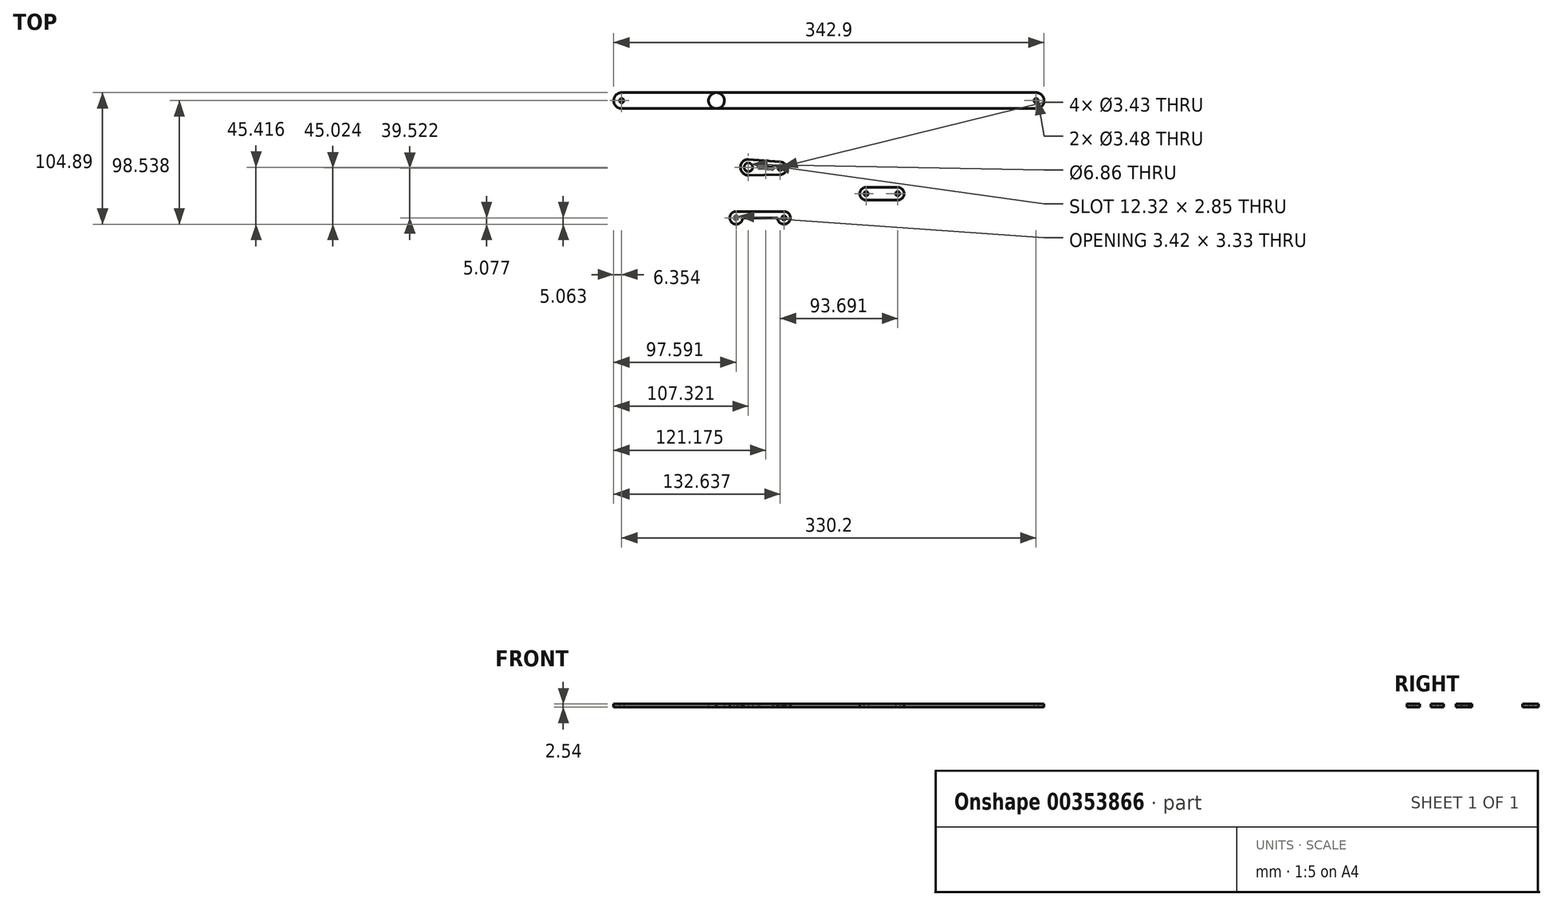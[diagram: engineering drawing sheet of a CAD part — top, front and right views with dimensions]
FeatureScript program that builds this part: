
annotation { "Feature Type Name" : "Feature", "Feature Type Description" : "" }
export const myFeature = defineFeature(function(context is Context, id is Id, definition is map)
    precondition{}
    {
        {
            var Q0;
            Q0=qCreatedBy(makeId("Top.planeOp"),FACE);
            var sketch = newSketch(context, id + "F0", { "sketchPlane" : qUnion([Q0])});
            skLineSegment(sketch, "E0", {"start": v(-140.79, 34.4) * mm, "end": v(189.41, 34.4) * mm});
            skCircle(sketch, "E1", {"center": v(-65.23, 34.4) * mm, "radius": 6.35 * mm});
            skCircle(sketch, "E2", {"center": v(-140.79, 34.4) * mm, "radius": 6.35 * mm});
            skCircle(sketch, "E3", {"center": v(189.41, 34.4) * mm, "radius": 6.35 * mm});
            skCircle(sketch, "E4", {"center": v(-140.79, 34.4) * mm, "radius": 1.74 * mm});
            skCircle(sketch, "E5", {"center": v(-65.23, 34.4) * mm, "radius": 1.74 * mm});
            skCircle(sketch, "E6", {"center": v(189.41, 34.4) * mm, "radius": 1.74 * mm});
            skLineSegment(sketch, "E7", {"start": v(-140.74, 40.75) * mm, "end": v(-65.23, 40.75) * mm});
            skLineSegment(sketch, "E8", {"start": v(-65.23, 40.75) * mm, "end": v(189.41, 40.75) * mm});
            skLineSegment(sketch, "E9", {"start": v(-140.79, 28.05) * mm, "end": v(189.41, 28.05) * mm});
            skSolve(sketch);
        }
        {
            var Q0;
            {var subQ5=sQuery(id+"F0.wireOp",EDGE,"omyWqJSU-xpnl-p9V4-5C7R-NGolSmvEfpRZ");Q0=makeQuery(id+"F0.imprint","IMPRINT",FACE,{"disambiguationData":[TD([[makeQuery(id+"F0.imprint","IMPRINT",EDGE,{"derivedFrom":subQ5}),-1.0]])]});}
            var Q1;
            {var subQ5=sQuery(id+"F0.wireOp",EDGE,"3vT1Dh1F-cFY9-jmHm-KNHv-sDzjYtVH3cF0");Q1=makeQuery(id+"F0.imprint","IMPRINT",FACE,{"disambiguationData":[TD([[makeQuery(id+"F0.imprint","IMPRINT",EDGE,{"derivedFrom":subQ5}),-1.0]])]});}
            var Q2;
            {var subQ5=sQuery(id+"F0.wireOp",EDGE,"hbOdxzbA-R3wx-VJPs-SB4o-o1RYoFjZylJU");Q2=makeQuery(id+"F0.imprint","IMPRINT",FACE,{"disambiguationData":[TD([[makeQuery(id+"F0.imprint","IMPRINT",EDGE,{"derivedFrom":subQ5}),1.0]])]});}
            var Q3;
            {var subQ5=sQuery(id+"F0.wireOp",EDGE,"hi4iPLOx-z5Hb-Hoi3-IES0-81KWlargqKwF");Q3=makeQuery(id+"F0.imprint","IMPRINT",FACE,{"disambiguationData":[TD([[makeQuery(id+"F0.imprint","IMPRINT",EDGE,{"derivedFrom":subQ5}),-1.0]])]});}
            var Q4;
            {var subQ0=sQuery(id+"F0.wireOp",EDGE,"E1");var subQ3=sQuery(id+"F0.wireOp",EDGE,"E0");var subQ4=makeQuery(id+"F0.imprint","INTERSECT",VERTEX,{"disambiguationData":[OD(0.0)],"derivedFrom":[subQ3,subQ0]});Q4=makeQuery(id+"F0.imprint","IMPRINT",FACE,{"disambiguationData":[TD([[makeQuery(id+"F0.imprint","IMPRINT",EDGE,{"disambiguationData":[TD([[subQ4,-1.0]])],"derivedFrom":subQ3}),-1.0]])]});}
            var Q5;
            {var subQ0=sQuery(id+"F0.wireOp",EDGE,"E1");var subQ2=sQuery(id+"F0.wireOp",EDGE,"E0");var subQ7=makeQuery(id+"F0.imprint","INTERSECT",VERTEX,{"disambiguationData":[OD(0.0)],"derivedFrom":[subQ2,subQ0]});Q5=makeQuery(id+"F0.imprint","IMPRINT",FACE,{"disambiguationData":[TD([[makeQuery(id+"F0.imprint","IMPRINT",EDGE,{"disambiguationData":[TD([[subQ7,-1.0]])],"derivedFrom":subQ2}),1.0]])]});}
            var Q6;
            Q6=makeQuery(id+"F0.imprint","IMPRINT",FACE,{"disambiguationData":[TD([[makeQuery(id+"F0.imprint","IMPRINT",EDGE,{"derivedFrom":sQuery(id+"F0.wireOp",EDGE,"E4")}),-1.0]])]});
            var Q7;
            Q7=makeQuery(id+"F0.imprint","IMPRINT",FACE,{"disambiguationData":[TD([[makeQuery(id+"F0.imprint","IMPRINT",EDGE,{"derivedFrom":sQuery(id+"F0.wireOp",EDGE,"E6")}),-1.0]])]});
            var Q8;
            {var subQ0=sQuery(id+"F0.wireOp",EDGE,"E2");var subQ1=sQuery(id+"F0.wireOp",EDGE,"E0");var subQ2=makeQuery(id+"F0.imprint","INTERSECT",VERTEX,{"derivedFrom":[subQ1,subQ0]});Q8=makeQuery(id+"F0.imprint","IMPRINT",FACE,{"disambiguationData":[TD([[makeQuery(id+"F0.imprint","IMPRINT",EDGE,{"disambiguationData":[TD([[subQ2,-1.0]])],"derivedFrom":subQ1}),-1.0]])]});}
            var Q9;
            {var subQ5=sQuery(id+"F0.wireOp",EDGE,"E7");Q9=makeQuery(id+"F0.imprint","IMPRINT",FACE,{"disambiguationData":[TD([[makeQuery(id+"F0.imprint","IMPRINT",EDGE,{"derivedFrom":subQ5}),-1.0]])]});}
            var Q10;
            {var subQ0=sQuery(id+"F0.wireOp",EDGE,"E3");var subQ1=sQuery(id+"F0.wireOp",EDGE,"E0");var subQ2=makeQuery(id+"F0.imprint","INTERSECT",VERTEX,{"derivedFrom":[subQ1,subQ0]});Q10=makeQuery(id+"F0.imprint","IMPRINT",FACE,{"disambiguationData":[TD([[makeQuery(id+"F0.imprint","IMPRINT",EDGE,{"disambiguationData":[TD([[subQ2,1.0]])],"derivedFrom":subQ1}),-1.0]])]});}
            var Q11;
            {var subQ5=sQuery(id+"F0.wireOp",EDGE,"E8");Q11=makeQuery(id+"F0.imprint","IMPRINT",FACE,{"disambiguationData":[TD([[makeQuery(id+"F0.imprint","IMPRINT",EDGE,{"derivedFrom":subQ5}),-1.0]])]});}
            extrude(context, id + "F1", {"entities" : qUnion([Q0, Q1, Q2, Q3, Q4, Q5, Q6, Q7, Q8, Q9, Q10, Q11]), "depth" : 2.54 * mm});
        }
        {
            var Q0;
            Q0=qCreatedBy(makeId("Top.planeOp"),FACE);
            var sketch = newSketch(context, id + "F2", { "sketchPlane" : qUnion([Q0])});
            skCircle(sketch, "E10", {"center": v(-39.82, -18.72) * mm, "radius": 6.35 * mm});
            skCircle(sketch, "E11", {"center": v(-14.5, -19.54) * mm, "radius": 5.08 * mm});
            skLineSegment(sketch, "E12", {"start": v(-39.9, -25.07) * mm, "end": v(-14.5, -24.62) * mm});
            skLineSegment(sketch, "E13", {"start": v(-39.82, -12.37) * mm, "end": v(-14.5, -14.44) * mm});
            skCircle(sketch, "E14", {"center": v(-39.82, -18.72) * mm, "radius": 3.43 * mm});
            skCircle(sketch, "E15", {"center": v(-14.5, -19.54) * mm, "radius": 1.71 * mm});
            skLineSegment(sketch, "E16", {"start": v(-39.9, -25.07) * mm, "end": v(-39.82, -12.37) * mm});
            skLineSegment(sketch, "E17", {"start": v(-14.5, -24.62) * mm, "end": v(-14.5, -14.44) * mm});
            skCircle(sketch, "E18", {"center": v(-20.81, -19.54) * mm, "radius": 1.02 * mm});
            skCircle(sketch, "E19", {"center": v(-31.1, -18.7) * mm, "radius": 1.02 * mm});
            skLineSegment(sketch, "E20", {"start": v(-31, -17.69) * mm, "end": v(-20.73, -18.53) * mm});
            skLineSegment(sketch, "E21", {"start": v(-20.73, -18.53) * mm, "end": v(-20.81, -20.56) * mm});
            skLineSegment(sketch, "E22", {"start": v(-20.81, -20.56) * mm, "end": v(-31, -19.71) * mm});
            skLineSegment(sketch, "E23", {"start": v(-31, -19.71) * mm, "end": v(-31, -17.69) * mm});
            skSolve(sketch);
        }
        {
            var Q0;
            {var subQ1=sQuery(id+"F2.wireOp",EDGE,"E13");var subQ3=sQuery(id+"F2.wireOp",EDGE,"E10");var subQ4=makeQuery(id+"F2.imprint","INTERSECT",VERTEX,{"derivedFrom":[subQ3,subQ1]});Q0=makeQuery(id+"F2.imprint","IMPRINT",FACE,{"disambiguationData":[TD([[makeQuery(id+"F2.imprint","IMPRINT",EDGE,{"disambiguationData":[TD([[subQ4,1.0]])],"derivedFrom":subQ3}),-1.0]])]});}
            var Q1;
            {var subQ0=sQuery(id+"F2.wireOp",EDGE,"E16");var subQ4=sQuery(id+"F2.wireOp",EDGE,"E14");var subQ6=makeQuery(id+"F2.imprint","INTERSECT",VERTEX,{"disambiguationData":[OD(0.0)],"derivedFrom":[subQ4,subQ0]});Q1=makeQuery(id+"F2.imprint","IMPRINT",FACE,{"disambiguationData":[TD([[makeQuery(id+"F2.imprint","IMPRINT",EDGE,{"disambiguationData":[TD([[subQ6,1.0]])],"derivedFrom":subQ4}),-1.0]])]});}
            var Q2;
            {var subQ1=sQuery(id+"F2.wireOp",EDGE,"E13");var subQ2=sQuery(id+"F2.wireOp",EDGE,"E10");var subQ4=makeQuery(id+"F2.imprint","INTERSECT",VERTEX,{"derivedFrom":[subQ2,subQ1]});Q2=makeQuery(id+"F2.imprint","IMPRINT",FACE,{"disambiguationData":[TD([[makeQuery(id+"F2.imprint","IMPRINT",EDGE,{"disambiguationData":[TD([[subQ4,1.0]])],"derivedFrom":subQ2}),1.0]])]});}
            var Q3;
            {var subQ0=sQuery(id+"F2.wireOp",EDGE,"E17");var subQ4=sQuery(id+"F2.wireOp",EDGE,"E15");var subQ5=makeQuery(id+"F2.imprint","INTERSECT",VERTEX,{"disambiguationData":[OD(0.0)],"derivedFrom":[subQ4,subQ0]});Q3=makeQuery(id+"F2.imprint","IMPRINT",FACE,{"disambiguationData":[TD([[makeQuery(id+"F2.imprint","IMPRINT",EDGE,{"disambiguationData":[TD([[subQ5,-1.0]])],"derivedFrom":subQ4}),-1.0]])]});}
            var Q4;
            {var subQ0=sQuery(id+"F2.wireOp",EDGE,"E17");var subQ4=sQuery(id+"F2.wireOp",EDGE,"E15");var subQ5=makeQuery(id+"F2.imprint","INTERSECT",VERTEX,{"disambiguationData":[OD(0.0)],"derivedFrom":[subQ4,subQ0]});Q4=makeQuery(id+"F2.imprint","IMPRINT",FACE,{"disambiguationData":[TD([[makeQuery(id+"F2.imprint","IMPRINT",EDGE,{"disambiguationData":[TD([[subQ5,1.0]])],"derivedFrom":subQ4}),-1.0]])]});}
            extrude(context, id + "F3", {"entities" : qUnion([Q0, Q1, Q2, Q3, Q4]), "depth" : 2.54 * mm});
        }
        {
            var Q0;
            Q0=qCreatedBy(makeId("Top.planeOp"),FACE);
            var sketch = newSketch(context, id + "F4", { "sketchPlane" : qUnion([Q0])});
            skLineSegment(sketch, "E24", {"start": v(53.93, -39.78) * mm, "end": v(79.19, -39.78) * mm});
            skCircle(sketch, "E25", {"center": v(53.93, -39.78) * mm, "radius": 5.08 * mm});
            skCircle(sketch, "E26", {"center": v(79.19, -39.78) * mm, "radius": 5.08 * mm});
            skLineSegment(sketch, "E27", {"start": v(53.93, -34.7) * mm, "end": v(79.19, -34.7) * mm});
            skLineSegment(sketch, "E28", {"start": v(53.93, -44.86) * mm, "end": v(79.19, -44.86) * mm});
            skCircle(sketch, "E29", {"center": v(53.93, -39.78) * mm, "radius": 1.71 * mm});
            skCircle(sketch, "E30", {"center": v(79.19, -39.78) * mm, "radius": 1.71 * mm});
            skSolve(sketch);
        }
        {
            var Q0;
            Q0=makeQuery(id+"F4.imprint","IMPRINT",FACE,{"disambiguationData":[TD([[makeQuery(id+"F4.imprint","IMPRINT",EDGE,{"derivedFrom":sQuery(id+"F4.wireOp",EDGE,"E29")}),-1.0]])]});
            var Q1;
            {var subQ5=sQuery(id+"F4.wireOp",EDGE,"E27");Q1=makeQuery(id+"F4.imprint","IMPRINT",FACE,{"disambiguationData":[TD([[makeQuery(id+"F4.imprint","IMPRINT",EDGE,{"derivedFrom":subQ5}),-1.0]])]});}
            var Q2;
            {var subQ5=sQuery(id+"F4.wireOp",EDGE,"E28");Q2=makeQuery(id+"F4.imprint","IMPRINT",FACE,{"disambiguationData":[TD([[makeQuery(id+"F4.imprint","IMPRINT",EDGE,{"derivedFrom":subQ5}),1.0]])]});}
            var Q3;
            Q3=makeQuery(id+"F4.imprint","IMPRINT",FACE,{"disambiguationData":[TD([[makeQuery(id+"F4.imprint","IMPRINT",EDGE,{"derivedFrom":sQuery(id+"F4.wireOp",EDGE,"E30")}),-1.0]])]});
            extrude(context, id + "F5", {"entities" : qUnion([Q0, Q1, Q2, Q3]), "depth" : 2.54 * mm});
        }
        {
            var Q0;
            Q0=qCreatedBy(makeId("Top.planeOp"),FACE);
            var sketch = newSketch(context, id + "F6", { "sketchPlane" : qUnion([Q0])});
            skLineSegment(sketch, "E31", {"start": v(-49.55, -59.06) * mm, "end": v(-11.45, -59.06) * mm});
            skCircle(sketch, "E32", {"center": v(-11.45, -59.06) * mm, "radius": 1.71 * mm});
            skCircle(sketch, "E33", {"center": v(-49.55, -59.06) * mm, "radius": 1.71 * mm});
            skCircle(sketch, "E34", {"center": v(-49.55, -59.06) * mm, "radius": 5.08 * mm});
            skCircle(sketch, "E35", {"center": v(-11.45, -59.06) * mm, "radius": 5.08 * mm});
            skLineSegment(sketch, "E36", {"start": v(-49.4, -53.98) * mm, "end": v(-11.45, -53.98) * mm});
            skLineSegment(sketch, "E37", {"start": v(-11.01, -64.12) * mm, "end": v(-49.11, -64.12) * mm});
            skLineSegment(sketch, "E38", {"start": v(-49.11, -64.12) * mm, "end": v(-49.4, -53.98) * mm});
            skLineSegment(sketch, "E39", {"start": v(-11.01, -64.12) * mm, "end": v(-11.45, -53.98) * mm});
            skLineSegment(sketch, "E40", {"start": v(-47.84, -59.06) * mm, "end": v(-28.02, -59.06) * mm});
            skSolve(sketch);
        }
        {
            var Q0;
            {var subQ0=sQuery(id+"F6.wireOp",EDGE,"Bgpbz2Ld-bBj6-uYsi-zDKY-uDNDgDHbZwpL");var subQ1=sQuery(id+"F6.wireOp",EDGE,"E33");var subQ2=makeQuery(id+"F6.imprint","INTERSECT",VERTEX,{"derivedFrom":[subQ1,subQ0]});Q0=makeQuery(id+"F6.imprint","IMPRINT",FACE,{"disambiguationData":[TD([[makeQuery(id+"F6.imprint","IMPRINT",EDGE,{"disambiguationData":[TD([[subQ2,-1.0]])],"derivedFrom":subQ1}),-1.0]])]});}
            var Q1;
            {var subQ0=sQuery(id+"F6.wireOp",EDGE,"E33");var subQ1=sQuery(id+"F6.wireOp",EDGE,"E31");var subQ2=makeQuery(id+"F6.imprint","INTERSECT",VERTEX,{"derivedFrom":[subQ1,subQ0]});Q1=makeQuery(id+"F6.imprint","IMPRINT",FACE,{"disambiguationData":[TD([[makeQuery(id+"F6.imprint","IMPRINT",EDGE,{"disambiguationData":[TD([[subQ2,-1.0]])],"derivedFrom":subQ1}),1.0]])]});}
            var Q2;
            {var subQ0=sQuery(id+"F6.wireOp",EDGE,"E33");var subQ1=sQuery(id+"F6.wireOp",EDGE,"E31");var subQ2=makeQuery(id+"F6.imprint","INTERSECT",VERTEX,{"derivedFrom":[subQ1,subQ0]});Q2=makeQuery(id+"F6.imprint","IMPRINT",FACE,{"disambiguationData":[TD([[makeQuery(id+"F6.imprint","IMPRINT",EDGE,{"disambiguationData":[TD([[subQ2,-1.0]])],"derivedFrom":subQ1}),-1.0]])]});}
            var Q3;
            {var subQ0=sQuery(id+"F6.wireOp",EDGE,"E32");var subQ1=sQuery(id+"F6.wireOp",EDGE,"E31");var subQ2=makeQuery(id+"F6.imprint","INTERSECT",VERTEX,{"derivedFrom":[subQ1,subQ0]});Q3=makeQuery(id+"F6.imprint","IMPRINT",FACE,{"disambiguationData":[TD([[makeQuery(id+"F6.imprint","IMPRINT",EDGE,{"disambiguationData":[TD([[subQ2,1.0]])],"derivedFrom":subQ1}),-1.0]])]});}
            var Q4;
            {var subQ0=sQuery(id+"F6.wireOp",EDGE,"E32");var subQ1=sQuery(id+"F6.wireOp",EDGE,"E31");var subQ2=makeQuery(id+"F6.imprint","INTERSECT",VERTEX,{"derivedFrom":[subQ1,subQ0]});Q4=makeQuery(id+"F6.imprint","IMPRINT",FACE,{"disambiguationData":[TD([[makeQuery(id+"F6.imprint","IMPRINT",EDGE,{"disambiguationData":[TD([[subQ2,1.0]])],"derivedFrom":subQ1}),1.0]])]});}
            var Q5;
            {var subQ0=sQuery(id+"F6.wireOp",EDGE,"Bgpbz2Ld-bBj6-uYsi-zDKY-uDNDgDHbZwpL");var subQ1=sQuery(id+"F6.wireOp",EDGE,"E32");var subQ2=makeQuery(id+"F6.imprint","INTERSECT",VERTEX,{"derivedFrom":[subQ1,subQ0]});Q5=makeQuery(id+"F6.imprint","IMPRINT",FACE,{"disambiguationData":[TD([[makeQuery(id+"F6.imprint","IMPRINT",EDGE,{"disambiguationData":[TD([[subQ2,1.0]])],"derivedFrom":subQ1}),-1.0]])]});}
            var Q6;
            {var subQ11=sQuery(id+"F6.wireOp",EDGE,"U45tlp8s-4OnP-wPe7-IWFw-RmwRC4J37IfR");Q6=makeQuery(id+"F6.imprint","IMPRINT",FACE,{"disambiguationData":[TD([[makeQuery(id+"F6.imprint","IMPRINT",EDGE,{"derivedFrom":subQ11}),1.0]])]});}
            var Q7;
            {var subQ0=sQuery(id+"F6.wireOp",EDGE,"E36");Q7=makeQuery(id+"F6.imprint","IMPRINT",FACE,{"disambiguationData":[TD([[makeQuery(id+"F6.imprint","IMPRINT",EDGE,{"derivedFrom":subQ0}),-1.0]])]});}
            var Q8;
            {var subQ1=sQuery(id+"F6.wireOp",EDGE,"E34");var subQ5=sQuery(id+"F6.wireOp",EDGE,"ZXoGqPHU-PQwD-s1F0-fu0X-5xHNYyIfvDHT");var subQ6=makeQuery(id+"F6.imprint","INTERSECT",VERTEX,{"disambiguationData":[OD(1.0)],"derivedFrom":[subQ1,subQ5]});Q8=makeQuery(id+"F6.imprint","IMPRINT",FACE,{"disambiguationData":[TD([[makeQuery(id+"F6.imprint","IMPRINT",EDGE,{"disambiguationData":[TD([[subQ6,1.0]])],"derivedFrom":subQ5}),-1.0]])]});}
            var Q9;
            {var subQ3=sQuery(id+"F6.wireOp",EDGE,"ZXoGqPHU-PQwD-s1F0-fu0X-5xHNYyIfvDHT");var subQ7=sQuery(id+"F6.wireOp",EDGE,"E34");var subQ8=makeQuery(id+"F6.imprint","INTERSECT",VERTEX,{"disambiguationData":[OD(0.0)],"derivedFrom":[subQ7,subQ3]});Q9=makeQuery(id+"F6.imprint","IMPRINT",FACE,{"disambiguationData":[TD([[makeQuery(id+"F6.imprint","IMPRINT",EDGE,{"disambiguationData":[TD([[subQ8,-1.0]])],"derivedFrom":subQ3}),-1.0]])]});}
            var Q10;
            {var subQ1=sQuery(id+"F6.wireOp",EDGE,"E33");var subQ3=sQuery(id+"F6.wireOp",EDGE,"E38");var subQ4=makeQuery(id+"F6.imprint","INTERSECT",VERTEX,{"disambiguationData":[OD(0.0)],"derivedFrom":[subQ1,subQ3]});Q10=makeQuery(id+"F6.imprint","IMPRINT",FACE,{"disambiguationData":[TD([[makeQuery(id+"F6.imprint","IMPRINT",EDGE,{"disambiguationData":[TD([[subQ4,1.0]])],"derivedFrom":subQ1}),-1.0]])]});}
            var Q11;
            {var subQ5=sQuery(id+"F6.wireOp",EDGE,"E31");var subQ7=sQuery(id+"F6.wireOp",EDGE,"E40");var subQ9=makeQuery(id+"F6.imprint","INTERSECT",VERTEX,{"derivedFrom":[subQ5,subQ7]});Q11=makeQuery(id+"F6.imprint","IMPRINT",FACE,{"disambiguationData":[TD([[makeQuery(id+"F6.imprint","IMPRINT",EDGE,{"disambiguationData":[TD([[subQ9,-1.0]])],"derivedFrom":subQ5}),-1.0]])]});}
            extrude(context, id + "F7", {"entities" : qUnion([Q0, Q1, Q2, Q3, Q4, Q5, Q6, Q7, Q8, Q9, Q10, Q11]), "depth" : 2.54 * mm});
        }
    });
